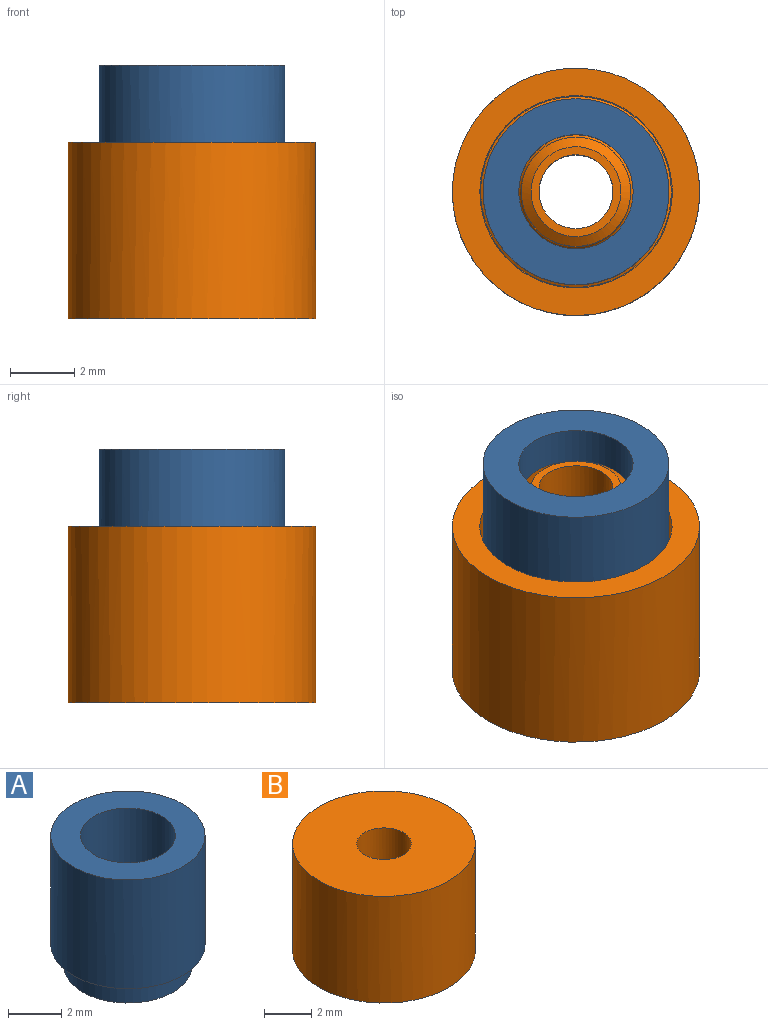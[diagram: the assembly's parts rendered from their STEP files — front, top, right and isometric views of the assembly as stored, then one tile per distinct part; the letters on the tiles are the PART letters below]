
ASSEMBLY  parts=2 mates=1
PART A: 7 faces, bbox 5.8x5.8x6 mm
  f0: cylinder r=2.89mm len=5.79mm, axis (0,0,-1), area 90.8mm2, adj f3,f4
  f1: plane 4.8x4.8mm, normal (0,0,-1), area 5.1mm2, adj f5,f6
  f2: cylinder r=1.78mm len=5.75mm, axis (0,0,-1), area 64.3mm2, adj f3,f6
  f3: plane 5.79x5.79mm, normal (0,0,1), area 16.4mm2, adj f0,f2
  f4: plane 5.79x5.79mm, normal (0,0,-1), area 8.2mm2, adj f0,f5
  f5: cylinder r=2.4mm len=4.8mm, axis (0,0,-1), area 15.2mm2, adj f1,f4
  f6: cone r=2.03mm half-angle=45deg, axis (0,0,-1), area 4.2mm2, adj f1,f2
PART B: 15 faces, bbox 7.7x7.7x7 mm
  f0: cylinder r=3.85mm len=7.7mm, axis (0,0,-1), area 133mm2, adj f2,f4
  f1: plane 2.8x2.8mm, normal (0,0,-1), area 2mm2, adj f3,f12
  f2: plane 7.7x7.7mm, normal (0,0,1), area 42.4mm2, adj f0,f3
  f3: cylinder r=1.15mm len=7mm, axis (0,0,-1), area 50.6mm2, adj f1,f2
  f4: plane 7.7x7.7mm, normal (0,0,-1), area 18.4mm2, adj f0,f6
  f5: cylinder r=1.7mm len=6.09mm, axis (0,0,-1), area 65mm2, adj f12,f14
  f6: cylinder r=2.99mm len=5.99mm, axis (0,0,-1), area 48.9mm2, adj f4,f7
  f7: plane 5.99x5.99mm, normal (0,0,-1), area 0.5mm2, adj f6,f11
  f8: cylinder r=2.5mm len=5mm, axis (0,0,-1), area 34.6mm2, adj f10,f13
  f9: plane 4.6x4.6mm, normal (0,0,-1), area 5.3mm2, adj f13,f14
  f10: cone r=2.97mm half-angle=60deg, axis (0,0,1), area 9.3mm2, adj f8,f11
  f11: cylinder r=2.97mm len=5.94mm, axis (0,0,1), area 5.1mm2, adj f7,f10
  f12: cone r=1.4mm half-angle=55deg, axis (0,0,1), area 3.6mm2, adj f1,f5
  f13: torus R=2.3mm, axis (0,0,-1), area 4.8mm2, adj f8,f9
  f14: torus R=1.9mm, axis (0,0,-1), area 3.5mm2, adj f5,f9
PLACE A t=(5.6,3.24,6.38)mm
PLACE B rot(axis=(-1,0,0),180deg) t=(5.6,3.24,11.48)mm
MATE slider A.f0 <-> B.f0  axis (0,0,-1) through (5.6,3.24,9.89)mm
